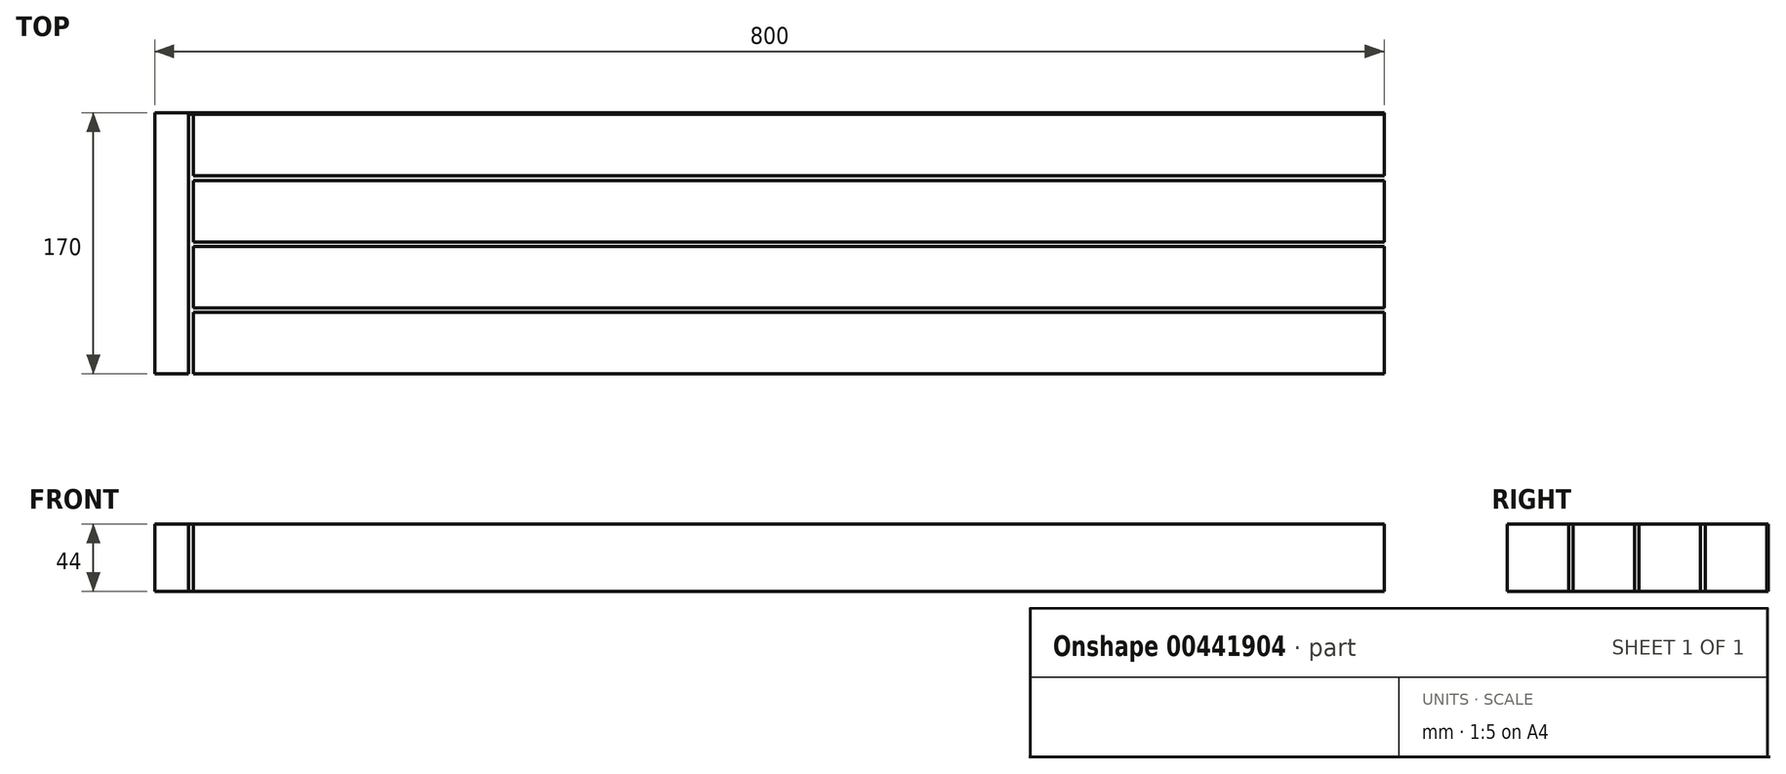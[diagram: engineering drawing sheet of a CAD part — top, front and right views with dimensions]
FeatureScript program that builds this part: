
annotation { "Feature Type Name" : "Feature", "Feature Type Description" : "" }
export const myFeature = defineFeature(function(context is Context, id is Id, definition is map)
    precondition{}
    {
        {
            var Q0;
            Q0=qCreatedBy(makeId("Top.planeOp"),FACE);
            var sketch = newSketch(context, id + "F0", { "sketchPlane" : qUnion([Q0])});
            skLineSegment(sketch, "E0.bottom", {"start": v(0, 0) * mm, "end": v(-800, 0) * mm});
            skLineSegment(sketch, "E0.top", {"start": v(0, 170) * mm, "end": v(-800, 170) * mm});
            skLineSegment(sketch, "E0.left", {"start": v(0, 0) * mm, "end": v(0, 170) * mm});
            skLineSegment(sketch, "E0.right", {"start": v(-800, 0) * mm, "end": v(-800, 170) * mm});
            skLineSegment(sketch, "E1", {"start": v(0, 0) * mm, "end": v(0, 40) * mm, "construction": true});
            skLineSegment(sketch, "E2", {"start": v(0, 40) * mm, "end": v(0, 43) * mm, "construction": true});
            skLineSegment(sketch, "E3", {"start": v(0, 43) * mm, "end": v(0, 83) * mm, "construction": true});
            skLineSegment(sketch, "E4", {"start": v(0, 86) * mm, "end": v(0, 126) * mm, "construction": true});
            skLineSegment(sketch, "E5", {"start": v(0, 126) * mm, "end": v(0, 129) * mm, "construction": true});
            skLineSegment(sketch, "E6", {"start": v(0, 129) * mm, "end": v(0, 169) * mm, "construction": true});
            skLineSegment(sketch, "E7.left", {"start": v(0, 40) * mm, "end": v(0, 43) * mm});
            skLineSegment(sketch, "E8.left", {"start": v(0, 83) * mm, "end": v(0, 86) * mm});
            skSolve(sketch);
        }
        {
            var Q0;
            Q0 = qSketchRegion(id + "F0", true);
            extrude(context, id + "F1", {"entities" : qUnion([Q0]), "depth" : 44 * mm});
        }
        {
            var Q0;
            Q0=qCreatedBy(makeId("Top.planeOp"),FACE);
            var sketch = newSketch(context, id + "F2", { "sketchPlane" : qUnion([Q0])});
            skLineSegment(sketch, "E9", {"start": v(0, 0) * mm, "end": v(0, 40) * mm, "construction": true});
            skLineSegment(sketch, "E10", {"start": v(0, 40) * mm, "end": v(0, 43) * mm, "construction": true});
            skLineSegment(sketch, "E11", {"start": v(0, 43) * mm, "end": v(0, 83) * mm, "construction": true});
            skLineSegment(sketch, "E12", {"start": v(0, 83) * mm, "end": v(0, 86) * mm, "construction": true});
            skLineSegment(sketch, "E13", {"start": v(0, 86) * mm, "end": v(0, 126) * mm, "construction": true});
            skLineSegment(sketch, "E14", {"start": v(0, 126) * mm, "end": v(0, 129) * mm, "construction": true});
            skLineSegment(sketch, "E15", {"start": v(0, 129) * mm, "end": v(0, 169) * mm, "construction": true});
            skLineSegment(sketch, "E16", {"start": v(0, 169) * mm, "end": v(-775, 169) * mm, "construction": true});
            skLineSegment(sketch, "E17.bottom", {"start": v(-775, 169) * mm, "end": v(-778, 169) * mm});
            skLineSegment(sketch, "E17.top", {"start": v(-775, 0) * mm, "end": v(-778, 0) * mm});
            skLineSegment(sketch, "E17.left", {"start": v(-775, 169) * mm, "end": v(-775, 0) * mm});
            skLineSegment(sketch, "E17.right", {"start": v(-778, 169) * mm, "end": v(-778, 0) * mm});
            skLineSegment(sketch, "E18.bottom", {"start": v(-775, 169) * mm, "end": v(0, 169) * mm});
            skLineSegment(sketch, "E18.top", {"start": v(-775, 169.5) * mm, "end": v(0, 169.5) * mm});
            skLineSegment(sketch, "E18.left", {"start": v(-775, 169) * mm, "end": v(-775, 169.5) * mm});
            skLineSegment(sketch, "E18.right", {"start": v(0, 169) * mm, "end": v(0, 169.5) * mm});
            skLineSegment(sketch, "E19.bottom", {"start": v(0, 126) * mm, "end": v(-775, 126) * mm});
            skLineSegment(sketch, "E19.top", {"start": v(0, 129) * mm, "end": v(-775, 129) * mm});
            skLineSegment(sketch, "E19.left", {"start": v(0, 126) * mm, "end": v(0, 129) * mm});
            skLineSegment(sketch, "E19.right", {"start": v(-775, 126) * mm, "end": v(-775, 129) * mm});
            skLineSegment(sketch, "E20.bottom", {"start": v(0, 83) * mm, "end": v(-775, 83) * mm});
            skLineSegment(sketch, "E20.top", {"start": v(0, 86) * mm, "end": v(-775, 86) * mm});
            skLineSegment(sketch, "E20.left", {"start": v(0, 83) * mm, "end": v(0, 86) * mm});
            skLineSegment(sketch, "E20.right", {"start": v(-775, 83) * mm, "end": v(-775, 86) * mm});
            skLineSegment(sketch, "E21.bottom", {"start": v(0, 40) * mm, "end": v(-775, 40) * mm});
            skLineSegment(sketch, "E21.top", {"start": v(0, 43) * mm, "end": v(-775, 43) * mm});
            skLineSegment(sketch, "E21.left", {"start": v(0, 40) * mm, "end": v(0, 43) * mm});
            skLineSegment(sketch, "E21.right", {"start": v(-775, 40) * mm, "end": v(-775, 43) * mm});
            skSolve(sketch);
        }
        {
            var Q0;
            Q0 = qSketchRegion(id + "F2", true);
            extrude(context, id + "F3", {"entities" : qUnion([Q0]), "operationType" : NewBodyOperationType.REMOVE, "depth" : 134 * mm});
        }
    });
